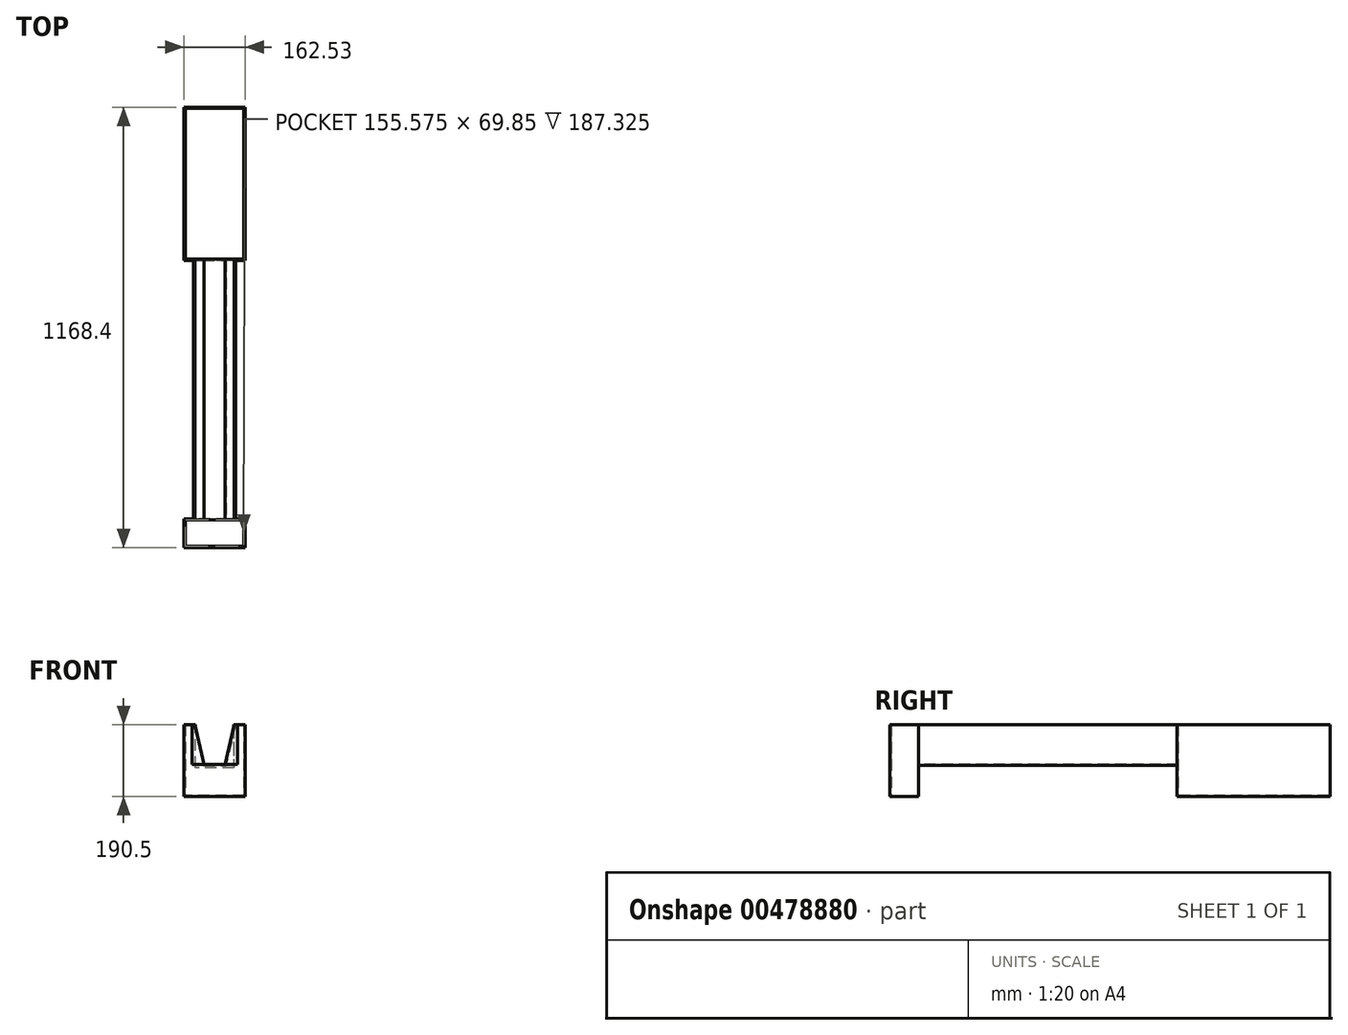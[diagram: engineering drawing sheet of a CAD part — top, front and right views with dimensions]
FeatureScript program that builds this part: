
annotation { "Feature Type Name" : "Feature", "Feature Type Description" : "" }
export const myFeature = defineFeature(function(context is Context, id is Id, definition is map)
    precondition{}
    {
        {
            var Q0;
            Q0=qCreatedBy(makeId("Front.planeOp"),FACE);
            var sketch = newSketch(context, id + "F0", { "sketchPlane" : qUnion([Q0])});
            skLineSegment(sketch, "E0", {"start": v(0, 0) * mm, "end": v(30.16, 0) * mm});
            skLineSegment(sketch, "E1", {"start": v(-30.16, 0) * mm, "end": v(0, 0) * mm});
            skLineSegment(sketch, "E2", {"start": v(-4.9, 107.95) * mm, "end": v(-55.56, 107.95) * mm});
            skLineSegment(sketch, "E3", {"start": v(-55.56, 107.95) * mm, "end": v(-30.16, 0) * mm});
            skLineSegment(sketch, "E4", {"start": v(-4.9, 107.95) * mm, "end": v(55.56, 107.95) * mm});
            skLineSegment(sketch, "E5", {"start": v(55.56, 107.95) * mm, "end": v(30.16, 0) * mm});
            skSolve(sketch);
        }
        {
            var Q0;
            Q0 = qSketchRegion(id + "F0", true);
            extrude(context, id + "F1", {"entities" : qUnion([Q0]), "oppositeDirection" : true, "depth" : 685.8 * mm, "offsetDistance" : 25.4 * mm});
        }
        {
            var Q0;
            Q0=makeQuery(id+"F1.opExtrude","CAP_FACE",FACE,{"disambiguationData":[OSD([sQuery(id+"F0.wireOp",EDGE,"E0"),sQuery(id+"F0.wireOp",EDGE,"AymDDnWp-5r5O-VMDs-1fak-TFMivUKxmNFS"),sQuery(id+"F0.wireOp",EDGE,"4GjVyFaO-0ejx-zzn4-fvXE-cH60FLfIHNaX"),sQuery(id+"F0.wireOp",EDGE,"JNnCu4fc-VA1w-Xx27-tmor-RhRPpysEvMKi"),sQuery(id+"F0.wireOp",EDGE,"E1")])],"isStart":true});
            var sketch = newSketch(context, id + "F2", { "sketchPlane" : qUnion([Q0])});
            skLineSegment(sketch, "E6", {"start": v(80.96, 107.95) * mm, "end": v(80.96, -82.55) * mm});
            skLineSegment(sketch, "E7", {"start": v(80.96, -82.55) * mm, "end": v(-80.96, -82.55) * mm});
            skLineSegment(sketch, "E8", {"start": v(0, 0) * mm, "end": v(-80.96, 0) * mm});
            skLineSegment(sketch, "E9", {"start": v(-80.96, 0) * mm, "end": v(-80.96, -82.55) * mm});
            skLineSegment(sketch, "E10", {"start": v(-80.96, 107.95) * mm, "end": v(80.96, 107.95) * mm});
            skLineSegment(sketch, "E11", {"start": v(-80.96, 107.95) * mm, "end": v(-80.96, 0) * mm});
            skSolve(sketch);
        }
        {
            var Q0;
            Q0 = qSketchRegion(id + "F2", true);
            extrude(context, id + "F3", {"entities" : qUnion([Q0]), "operationType" : NewBodyOperationType.ADD, "depth" : 76.2 * mm, "offsetDistance" : 25.4 * mm});
        }
        {
            var Q0;
            Q0=makeQuery(id+"F1.opExtrude","CAP_FACE",FACE,{"disambiguationData":[OSD([sQuery(id+"F0.wireOp",EDGE,"E0"),sQuery(id+"F0.wireOp",EDGE,"AymDDnWp-5r5O-VMDs-1fak-TFMivUKxmNFS"),sQuery(id+"F0.wireOp",EDGE,"4GjVyFaO-0ejx-zzn4-fvXE-cH60FLfIHNaX"),sQuery(id+"F0.wireOp",EDGE,"JNnCu4fc-VA1w-Xx27-tmor-RhRPpysEvMKi"),sQuery(id+"F0.wireOp",EDGE,"E1")])],"isStart":false});
            var sketch = newSketch(context, id + "F4", { "sketchPlane" : qUnion([Q0])});
            skLineSegment(sketch, "E12", {"start": v(-80.96, 107.95) * mm, "end": v(-80.96, -82.55) * mm});
            skLineSegment(sketch, "E13", {"start": v(-80.96, -82.55) * mm, "end": v(81.57, -82.55) * mm});
            skLineSegment(sketch, "E14", {"start": v(-80.96, 107.95) * mm, "end": v(80.96, 107.95) * mm});
            skLineSegment(sketch, "E15", {"start": v(80.96, 107.95) * mm, "end": v(81.57, -82.55) * mm});
            skSolve(sketch);
        }
        {
            var Q0;
            Q0 = qSketchRegion(id + "F4", true);
            extrude(context, id + "F5", {"entities" : qUnion([Q0]), "operationType" : NewBodyOperationType.ADD, "depth" : 406.4 * mm, "offsetDistance" : 25.4 * mm});
        }
        {
            var Q0;
            Q0=makeQuery(id+"F5.boolean.opBoolean","MERGE",FACE,{"derivedFrom":[makeQuery(id+"F3.boolean.opBoolean","MERGE",FACE,{"derivedFrom":[makeQuery(id+"F1.opExtrude","SWEPT_FACE",FACE,{"disambiguationData":[OSD([sQuery(id+"F0.wireOp",EDGE,"E2"),sQuery(id+"F0.wireOp",EDGE,"E4")])]}),makeQuery(id+"F3.opExtrude","SWEPT_FACE",FACE,{"disambiguationData":[OSD([sQuery(id+"F2.wireOp",EDGE,"E10")])]})]}),makeQuery(id+"F5.opExtrude","SWEPT_FACE",FACE,{"disambiguationData":[OSD([sQuery(id+"F4.wireOp",EDGE,"E14")])]})]});
            shell(context, id + "F6", {"entities" : qUnion([Q0]), "thickness" : 3.17 * mm});
        }
        {
            var Q0;
            Q0=makeQuery(id+"F5.opExtrude","CAP_FACE",FACE,{"disambiguationData":[OSD([sQuery(id+"F4.wireOp",EDGE,"E12"),sQuery(id+"F4.wireOp",EDGE,"E13"),sQuery(id+"F4.wireOp",EDGE,"E14"),sQuery(id+"F4.wireOp",EDGE,"E15")])],"isStart":false});
            var sketch = newSketch(context, id + "F7", { "sketchPlane" : qUnion([Q0])});
            skLineSegment(sketch, "E16", {"start": v(-50.8, 107.95) * mm, "end": v(-50.8, -6.35) * mm});
            skLineSegment(sketch, "E17", {"start": v(-50.8, -6.35) * mm, "end": v(50.8, -6.35) * mm});
            skLineSegment(sketch, "E18", {"start": v(50.8, -6.35) * mm, "end": v(50.8, 107.95) * mm});
            skLineSegment(sketch, "E19", {"start": v(50.8, 107.95) * mm, "end": v(-50.8, 107.95) * mm});
            skLineSegment(sketch, "E20", {"start": v(0, 0) * mm, "end": v(0, -6.35) * mm});
            skLineSegment(sketch, "E21", {"start": v(0, -6.35) * mm, "end": v(0, 0) * mm});
            skLineSegment(sketch, "E22", {"start": v(-50.8, 0) * mm, "end": v(0, 0) * mm});
            skSolve(sketch);
        }
        {
            var Q0;
            Q0 = qSketchRegion(id + "F7", true);
            extrude(context, id + "F8", {"entities" : qUnion([Q0]), "operationType" : NewBodyOperationType.REMOVE, "oppositeDirection" : true, "depth" : 25.4 * mm, "offsetDistance" : 25.4 * mm});
        }
        {
            var Q0;
            Q0=makeQuery(id+"F3.opExtrude","CAP_FACE",FACE,{"disambiguationData":[OSD([sQuery(id+"F2.wireOp",EDGE,"E6"),sQuery(id+"F2.wireOp",EDGE,"E7"),sQuery(id+"F2.wireOp",EDGE,"E9"),sQuery(id+"F2.wireOp",EDGE,"E10"),sQuery(id+"F2.wireOp",EDGE,"E11")])],"isStart":false});
            var sketch = newSketch(context, id + "F9", { "sketchPlane" : qUnion([Q0])});
            skLineSegment(sketch, "E23", {"start": v(0, 0) * mm, "end": v(0, 107.95) * mm});
            skLineSegment(sketch, "E24", {"start": v(0, 107.95) * mm, "end": v(-60.33, 107.95) * mm});
            skLineSegment(sketch, "E25", {"start": v(-60.33, 107.95) * mm, "end": v(-60.33, 3.17) * mm});
            skLineSegment(sketch, "E26", {"start": v(-60.33, 3.18) * mm, "end": v(60.33, 3.18) * mm});
            skLineSegment(sketch, "E27", {"start": v(60.33, 3.17) * mm, "end": v(60.33, 107.95) * mm});
            skLineSegment(sketch, "E28", {"start": v(60.33, 107.95) * mm, "end": v(0, 107.95) * mm});
            skSolve(sketch);
        }
        {
            var Q0;
            Q0 = qSketchRegion(id + "F9", true);
            extrude(context, id + "F10", {"entities" : qUnion([Q0]), "operationType" : NewBodyOperationType.REMOVE, "oppositeDirection" : true, "depth" : 25.4 * mm, "offsetDistance" : 25.4 * mm});
        }
    });
